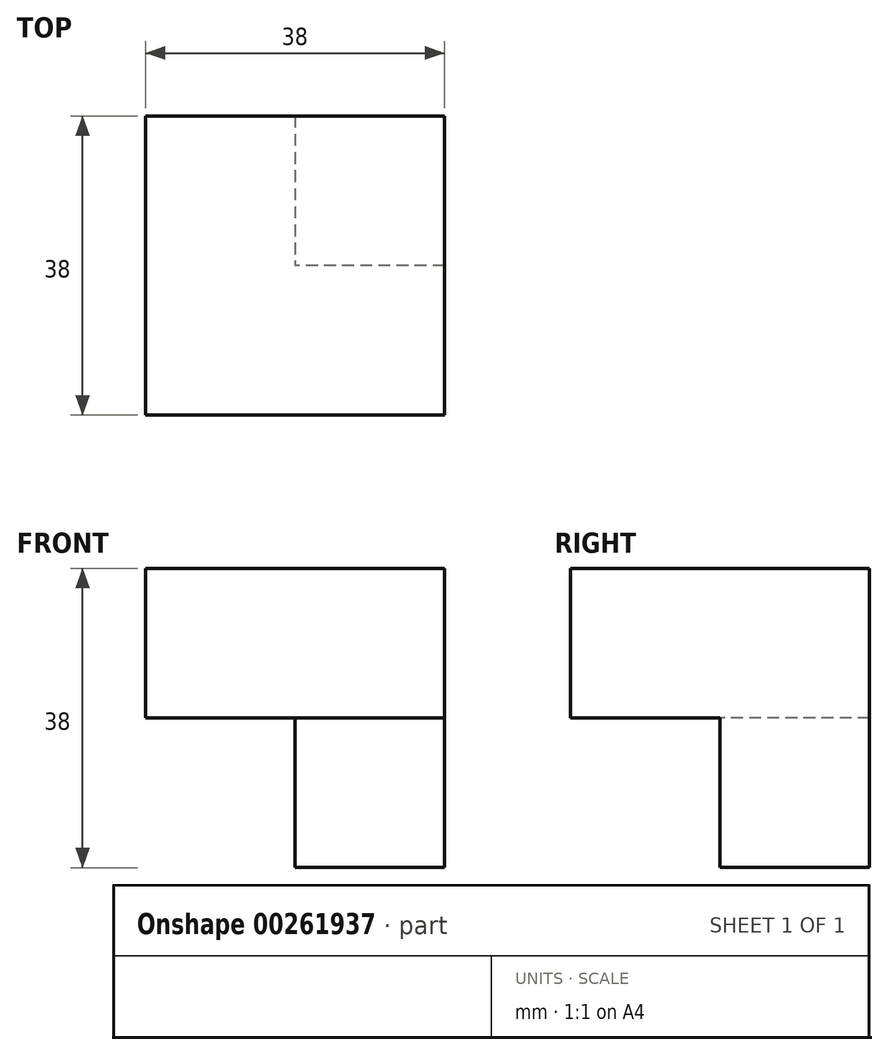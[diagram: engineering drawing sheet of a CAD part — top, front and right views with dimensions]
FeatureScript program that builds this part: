
annotation { "Feature Type Name" : "Feature", "Feature Type Description" : "" }
export const myFeature = defineFeature(function(context is Context, id is Id, definition is map)
    precondition{}
    {
        {
            var Q0;
            Q0=qCreatedBy(makeId("Top.planeOp"),FACE);
            var sketch = newSketch(context, id + "F0", { "sketchPlane" : qUnion([Q0])});
            skLineSegment(sketch, "E0.bottom", {"start": v(0, 0) * mm, "end": v(-19, 0) * mm});
            skLineSegment(sketch, "E0.top", {"start": v(0, 19) * mm, "end": v(-19, 19) * mm});
            skLineSegment(sketch, "E0.left", {"start": v(0, 0) * mm, "end": v(0, 19) * mm});
            skLineSegment(sketch, "E0.right", {"start": v(-19, 0) * mm, "end": v(-19, 19) * mm});
            skLineSegment(sketch, "E1.bottom", {"start": v(0, 19) * mm, "end": v(19, 19) * mm});
            skLineSegment(sketch, "E1.top", {"start": v(0, 0) * mm, "end": v(19, 0) * mm});
            skLineSegment(sketch, "E1.left", {"start": v(0, 19) * mm, "end": v(0, 0) * mm});
            skLineSegment(sketch, "E1.right", {"start": v(19, 19) * mm, "end": v(19, 0) * mm});
            skLineSegment(sketch, "E2.bottom", {"start": v(19, 0) * mm, "end": v(0, 0) * mm});
            skLineSegment(sketch, "E2.top", {"start": v(19, -19) * mm, "end": v(0, -19) * mm});
            skLineSegment(sketch, "E2.left", {"start": v(19, 0) * mm, "end": v(19, -19) * mm});
            skLineSegment(sketch, "E2.right", {"start": v(0, 0) * mm, "end": v(0, -19) * mm});
            skLineSegment(sketch, "E3.bottom", {"start": v(0, -19) * mm, "end": v(-19, -19) * mm});
            skLineSegment(sketch, "E3.left", {"start": v(0, -19) * mm, "end": v(0, 0) * mm});
            skLineSegment(sketch, "E3.right", {"start": v(-19, -19) * mm, "end": v(-19, 0) * mm});
            skSolve(sketch);
        }
        {
            var Q0;
            Q0=makeQuery(id+"F0.imprint","IMPRINT",FACE,{"disambiguationData":[TD([[makeQuery(id+"F0.imprint","IMPRINT",EDGE,{"derivedFrom":sQuery(id+"F0.wireOp",EDGE,"E1.bottom")}),-1.0]])]});
            extrude(context, id + "F1", {"entities" : qUnion([Q0]), "oppositeDirection" : true, "depth" : 38 * mm});
        }
        {
            var Q0;
            Q0 = qSketchRegion(id + "F0", true);
            extrude(context, id + "F2", {"entities" : qUnion([Q0]), "operationType" : NewBodyOperationType.ADD, "oppositeDirection" : true, "depth" : 19 * mm});
        }
    });
